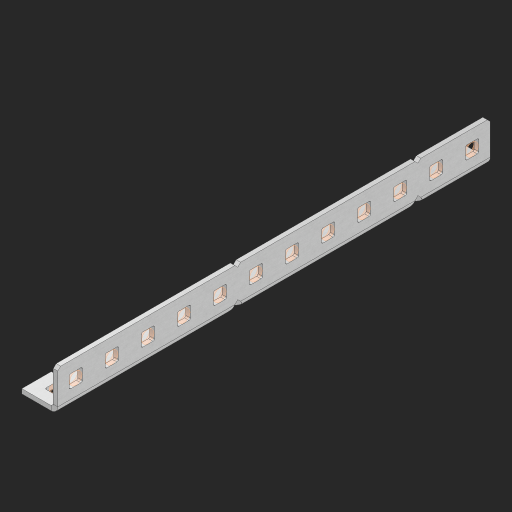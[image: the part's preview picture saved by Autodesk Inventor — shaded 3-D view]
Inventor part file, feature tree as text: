
AUTODESK INVENTOR PART (.ipt)
format: ipt  version: 2023 (Build 270158000, 158)  size: 774,656 bytes
history: native  units: in
note: dims shown in document units (in); Inventor stores cm internally (conversion verified against a paired STEP export)
features: other x184, extrude x34, sheet_metal_op x11, sketch x10, pattern_linear x2, mirror x1, chamfer x1
ambient origin geometry x8: Origin, YZ Plane, XZ Plane, XY Plane, X Axis, Y Axis, Z Axis, Center Point
bodies: Solid1 (feature_tree), Body (feature_tree)
feature tree (243):
  other  "Alu Half C 1x2x1x12"
  other  "Table"
  other  "Alu C 1x2x1x35"
  other  "Alu C 1x2x1x34"
  other  "Alu C 1x2x1x33"
  other  "Alu C 1x2x1x32"
  other  "Alu C 1x2x1x31"
  other  "Alu C 1x2x1x30"
  other  "Alu C 1x2x1x29"
  other  "Alu C 1x2x1x28"
  other  "Alu C 1x2x1x27"
  other  "Alu C 1x2x1x26"
  other  "Alu C 1x2x1x25"
  other  "Alu C 1x2x1x24"
  other  "Alu C 1x2x1x23"
  other  "Alu C 1x2x1x22"
  other  "Alu C 1x2x1x21"
  other  "Alu C 1x2x1x20"
  other  "Alu C 1x2x1x19"
  other  "Alu C 1x2x1x18"
  other  "Alu C 1x2x1x17"
  other  "Alu C 1x2x1x16"
  other  "Alu C 1x2x1x15"
  other  "Alu C 1x2x1x14"
  other  "Alu C 1x2x1x13"
  other  "Alu C 1x2x1x12"
  other  "Alu C 1x2x1x11"
  other  "Alu C 1x2x1x10"
  other  "Alu C 1x2x1x9"
  other  "Alu C 1x2x1x8"
  other  "Alu C 1x2x1x7"
  other  "Alu C 1x2x1x6"
  other  "Alu C 1x2x1x5"
  other  "Alu C 1x2x1x4"
  other  "Alu C 1x2x1x3"
  other  "Alu C 1x2x1x2"
  other  "Alu C 1x2x1x1"
  other  "Steel C 1x2x1x35"
  other  "Steel C 1x2x1x34"
  other  "Steel C 1x2x1x33"
  other  "Steel C 1x2x1x32"
  other  "Steel C 1x2x1x31"
  other  "Steel C 1x2x1x30"
  other  "Steel C 1x2x1x29"
  other  "Steel C 1x2x1x28"
  other  "Steel C 1x2x1x27"
  other  "Steel C 1x2x1x26"
  other  "Steel C 1x2x1x25"
  other  "Steel C 1x2x1x24"
  other  "Steel C 1x2x1x23"
  other  "Steel C 1x2x1x22"
  other  "Steel C 1x2x1x21"
  other  "Steel C 1x2x1x20"
  other  "Steel C 1x2x1x19"
  other  "Steel C 1x2x1x18"
  other  "Steel C 1x2x1x17"
  other  "Steel C 1x2x1x16"
  other  "Steel C 1x2x1x15"
  other  "Steel C 1x2x1x14"
  other  "Steel C 1x2x1x13"
  other  "Steel C 1x2x1x12"
  other  "Steel C 1x2x1x11"
  other  "Steel C 1x2x1x10"
  other  "Steel C 1x2x1x9"
  other  "Steel C 1x2x1x8"
  other  "Steel C 1x2x1x7"
  other  "Steel C 1x2x1x6"
  other  "Steel C 1x2x1x5"
  other  "Steel C 1x2x1x4"
  other  "Steel C 1x2x1x3"
  other  "Steel C 1x2x1x2"
  other  "Steel C 1x2x1x1"
  other  "Alu Half C 1x2x1x35"
  other  "Alu Half C 1x2x1x34"
  other  "Alu Half C 1x2x1x33"
  other  "Alu Half C 1x2x1x32"
  other  "Alu Half C 1x2x1x31"
  other  "Alu Half C 1x2x1x30"
  other  "Alu Half C 1x2x1x29"
  other  "Alu Half C 1x2x1x28"
  other  "Alu Half C 1x2x1x27"
  other  "Alu Half C 1x2x1x26"
  other  "Alu Half C 1x2x1x25"
  other  "Alu Half C 1x2x1x24"
  other  "Alu Half C 1x2x1x23"
  other  "Alu Half C 1x2x1x22"
  other  "Alu Half C 1x2x1x21"
  other  "Alu Half C 1x2x1x20"
  other  "Alu Half C 1x2x1x19"
  other  "Alu Half C 1x2x1x18"
  other  "Alu Half C 1x2x1x17"
  other  "Alu Half C 1x2x1x16"
  other  "Alu Half C 1x2x1x15"
  other  "Alu Half C 1x2x1x14"
  other  "Alu Half C 1x2x1x13"
  other  "Alu Half C 1x2x1x11"
  other  "Alu Half C 1x2x1x10"
  other  "Alu Half C 1x2x1x9"
  other  "Alu Half C 1x2x1x8"
  other  "Alu Half C 1x2x1x7"
  other  "Alu Half C 1x2x1x6"
  other  "Alu Half C 1x2x1x5"
  other  "Alu Half C 1x2x1x4"
  other  "Alu Half C 1x2x1x3"
  other  "Alu Half C 1x2x1x2"
  other  "Alu Half C 1x2x1x1"
  other  "Steel Half C 1x2x1x35"
  other  "Steel Half C 1x2x1x34"
  other  "Steel Half C 1x2x1x33"
  other  "Steel Half C 1x2x1x32"
  other  "Steel Half C 1x2x1x31"
  other  "Steel Half C 1x2x1x30"
  other  "Steel Half C 1x2x1x29"
  other  "Steel Half C 1x2x1x28"
  other  "Steel Half C 1x2x1x27"
  other  "Steel Half C 1x2x1x26"
  other  "Steel Half C 1x2x1x25"
  other  "Steel Half C 1x2x1x24"
  other  "Steel Half C 1x2x1x23"
  other  "Steel Half C 1x2x1x22"
  other  "Steel Half C 1x2x1x21"
  other  "Steel Half C 1x2x1x20"
  other  "Steel Half C 1x2x1x19"
  other  "Steel Half C 1x2x1x18"
  other  "Steel Half C 1x2x1x17"
  other  "Steel Half C 1x2x1x16"
  other  "Steel Half C 1x2x1x15"
  other  "Steel Half C 1x2x1x14"
  other  "Steel Half C 1x2x1x13"
  other  "Steel Half C 1x2x1x12"
  other  "Steel Half C 1x2x1x11"
  other  "Steel Half C 1x2x1x10"
  other  "Steel Half C 1x2x1x9"
  other  "Steel Half C 1x2x1x8"
  other  "Steel Half C 1x2x1x7"
  other  "Steel Half C 1x2x1x6"
  other  "Steel Half C 1x2x1x5"
  other  "Steel Half C 1x2x1x4"
  other  "Steel Half C 1x2x1x3"
  other  "Steel Half C 1x2x1x2"
  other  "Steel Half C 1x2x1x1"
  sheet_metal_op  "Flanges"
  other  "Flange Pattern Plane"
  other  "Flange Pattern Sketch"
  sheet_metal_op  "Flange Pattern"
  sheet_metal_op  "Body Pattern"
  pattern_linear  "Center Pattern"  Spacing1=0.0625in  [1 undecoded]
  other  "Arc Length"
  mirror  "Notch Mirror"
  pattern_linear  "Notch Pattern"  Spacing1=0.182in  [1 undecoded]
  chamfer  "End Chamfer"
  extrude  "Half Cut"  Depth=0.02in
  sketch  "Sketch1"  dims[d0=1.0in]
  other  "Plate1"
  sketch  "Sketch2"  dims[d1=6.0in]
  other  "Plate2"
  sheet_metal_op  "Bend1"
  sheet_metal_op  "Corner1"
  sketch  "Sketch3"  dims[d2=0.0625in]
  sketch  "Sketch7"  dims[d3=0.0625in]
  other  "Srf1"
  other  "Srf2"
  sketch  "Sketch8"  dims[d4=0.0312in]
  sketch  "Sketch9"  dims[d5=0.125in]
  other  "Srf91"
  sheet_metal_op  "Body Pattern Sketch"
  other  "Srf92"
  sketch  "Sketch13"  dims[d6=0.0625in]
  sketch  "Sketch14"  dims[d7=0.5in d8=90.0deg d9=0.0312in]
  sketch  "Sketch15"  dims[d10=0.25in]
  sketch  "Sketch16"  dims[d11=0.0625in d12=0.0625in d16=0.182in d17=0.02in d18=0.0625in d19=0.0in d20=0.25in d21=0.25in d38=4.7244in d40=0.5in d41=0.3937in d43=1.0in d46=0.172in d47=1.0in d48=0.0in d49=0.182in d50=0.02in d51=0.25in d52=0.25in d53=0.0625in d54=0.0in d55=0.172in d56=1.0in d57=0.0in d58=0.25in d60=4.7244in d62=0.5in d63=0.3937in d65=0.5in d85=0.1473in d86=0.1782in d88=0.04in d89=0.0625in d90=0.0in d91=0.04in d92=0.0491in d95=2.5in d96=0.04in d97=0.25in d98=45.0deg d99=0.25in d100=0.5in d101=0.0in d102=2.497in d106=0.182in d107=0.02in d108=0.5in d109=0.5in d110=0.0625in d111=0.0in d112=0.172in d113=0.5in d114=0.0in d117=0.5in d118=0.5in d119=0.5in]
  other  "Srf786"
  other  "Srf823"
  other  "Srf824"
  other  "Srf825"
  other  "Srf826"
  other  "Srf827"
  other  "Srf828"
  other  "Srf829"
  other  "Srf856"
  other  "Srf857"
  other  "Srf858"
  other  "Srf859"
  other  "Srf860"
  other  "Srf861"
  other  "Srf862"
  other  "Srf889"
  other  "Srf890"
  other  "Srf891"
  other  "Srf892"
  other  "Srf893"
  other  "Srf894"
  other  "Srf895"
  other  "Srf896"
  other  "Srf922"
  other  "Srf923"
  other  "Srf924"
  other  "Srf959"
  other  "Srf960"
  other  "Srf961"
  other  "Srf996"
  other  "Srf997"
  other  "Srf998"
  sheet_metal_op  "Flange Stamp"
  sheet_metal_op  "Flange Circle"
  sheet_metal_op  "Body Stamp"
  sheet_metal_op  "Body Circle"
  other  "Center Stamp"
  other  "Center Circle"
  sheet_metal_op  "Notch"
  extrude  "ExtrusionSrf2"  Depth=0.0625in
  extrude  "ExtrusionSrf92"  TaperAngle=0.0deg  [1 undecoded]
  extrude  "ExtrusionSrf823"  Depth=0.25in
  extrude  "ExtrusionSrf824"  Depth=0.25in
  extrude  "ExtrusionSrf825"  Depth=0.5in
  extrude  "ExtrusionSrf826"  Depth=0.5in
  extrude  "ExtrusionSrf827"  Depth=1.0in TaperAngle=0.0deg
  extrude  "ExtrusionSrf828"  Depth=0.182in
  extrude  "ExtrusionSrf829"  Depth=0.02in
  extrude  "ExtrusionSrf856"  Depth=0.25in
  extrude  "ExtrusionSrf857"  Depth=0.25in
  extrude  "ExtrusionSrf858"  Depth=0.0625in
  extrude  "ExtrusionSrf859"  TaperAngle=0.0deg  [1 undecoded]
  extrude  "ExtrusionSrf860"  Depth=0.5in
  extrude  "ExtrusionSrf861"  Depth=1.0in TaperAngle=0.0deg
  extrude  "ExtrusionSrf862"  Depth=0.25in
  extrude  "ExtrusionSrf889"  Depth=0.5in
  extrude  "ExtrusionSrf890"  Depth=0.5in
  extrude  "ExtrusionSrf891"  Depth=0.5in
  extrude  "ExtrusionSrf892"  Depth=0.5in
  extrude  "ExtrusionSrf893"  Depth=0.5in
  extrude  "ExtrusionSrf894"  Depth=0.0625in
  extrude  "ExtrusionSrf895"  TaperAngle=0.0deg  [1 undecoded]
  extrude  "ExtrusionSrf896"  Depth=0.5in
  extrude  "ExtrusionSrf922"  Depth=0.5in
  extrude  "ExtrusionSrf923"  Depth=2.5in
  extrude  "ExtrusionSrf924"  Depth=0.25in TaperAngle=45.0deg
  extrude  "ExtrusionSrf959"  Depth=0.25in
  extrude  "ExtrusionSrf960"  Depth=0.5in TaperAngle=0.0deg
  extrude  "ExtrusionSrf961"  Depth=0.5in
  extrude  "ExtrusionSrf996"  Depth=0.182in
  extrude  "ExtrusionSrf997"  Depth=0.02in
  extrude  "ExtrusionSrf998"  Depth=0.5in
note: 5 required parameter values undecoded (feature->parameter linkage not recoverable at this tier; creation-order binding heuristic only, values carry confidence <= 0.55)
